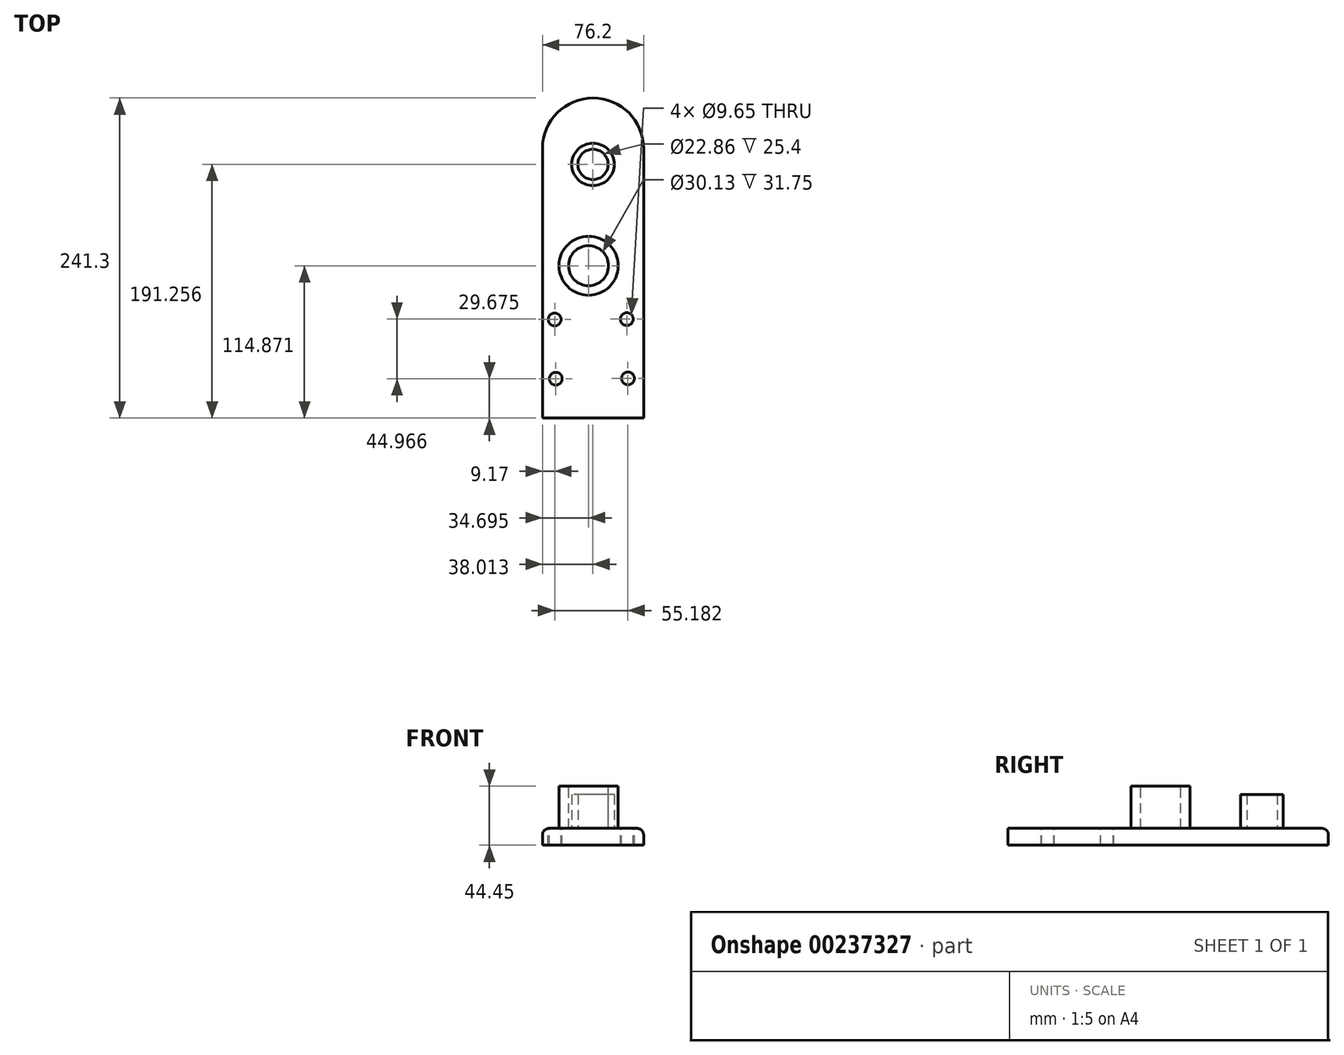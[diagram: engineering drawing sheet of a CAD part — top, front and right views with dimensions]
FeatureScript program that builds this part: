
annotation { "Feature Type Name" : "Feature", "Feature Type Description" : "" }
export const myFeature = defineFeature(function(context is Context, id is Id, definition is map)
    precondition{}
    {
        {
            var Q0;
            Q0=qCreatedBy(makeId("Top.planeOp"),FACE);
            var sketch = newSketch(context, id + "F0", { "sketchPlane" : qUnion([Q0])});
            skLineSegment(sketch, "E0", {"start": v(-28.8, -157.51) * mm, "end": v(47.4, -157.51) * mm});
            skLineSegment(sketch, "E1", {"start": v(47.4, -157.51) * mm, "end": v(47.4, 45.69) * mm});
            skLineSegment(sketch, "E2", {"start": v(-28.8, -157.51) * mm, "end": v(-28.8, 45.69) * mm});
            skArc(sketch, "E3", {"start": v(47.4, 45.69) * mm, "mid": v(9.3, 83.79) * mm, "end": v(-28.8, 45.69) * mm});
            skSolve(sketch);
        }
        {
            var Q0;
            Q0=makeQuery(id+"F0.imprint","IMPRINT",FACE,{"disambiguationData":[TD([[makeQuery(id+"F0.imprint","IMPRINT",EDGE,{"derivedFrom":sQuery(id+"F0.wireOp",EDGE,"E0")}),1.0]])]});
            extrude(context, id + "F1", {"entities" : qUnion([Q0]), "depth" : 12.7 * mm});
        }
        {
            var Q0;
            Q0=makeQuery(id+"F1.opExtrude","CAP_FACE",FACE,{"disambiguationData":[OSD([sQuery(id+"F0.wireOp",EDGE,"E0"),sQuery(id+"F0.wireOp",EDGE,"E1"),sQuery(id+"F0.wireOp",EDGE,"E2"),sQuery(id+"F0.wireOp",EDGE,"E3")])],"isStart":false});
            var sketch = newSketch(context, id + "F2", { "sketchPlane" : qUnion([Q0])});
            skCircle(sketch, "E4", {"center": v(-18.81, -127.83) * mm, "radius": 4.83 * mm});
            skCircle(sketch, "E5", {"center": v(35.54, -127.56) * mm, "radius": 4.83 * mm});
            skCircle(sketch, "E6", {"center": v(-19.64, -83.14) * mm, "radius": 4.83 * mm});
            skCircle(sketch, "E7", {"center": v(34.72, -82.87) * mm, "radius": 4.83 * mm});
            skSolve(sketch);
        }
        {
            var Q0;
            Q0 = qSketchRegion(id + "F2", true);
            extrude(context, id + "F3", {"entities" : qUnion([Q0]), "operationType" : NewBodyOperationType.REMOVE, "endBound" : BoundingType.THROUGH_ALL, "oppositeDirection" : true, "depth" : 25.4 * mm});
        }
        {
            var Q0;
            Q0=makeQuery(id+"F1.opExtrude","CAP_FACE",FACE,{"disambiguationData":[OSD([sQuery(id+"F0.wireOp",EDGE,"E0"),sQuery(id+"F0.wireOp",EDGE,"E1"),sQuery(id+"F0.wireOp",EDGE,"E2"),sQuery(id+"F0.wireOp",EDGE,"E3")])],"isStart":false});
            var sketch = newSketch(context, id + "F4", { "sketchPlane" : qUnion([Q0])});
            skCircle(sketch, "E8", {"center": v(5.88, -42.64) * mm, "radius": 22.23 * mm});
            skCircle(sketch, "E9", {"center": v(5.88, -42.64) * mm, "radius": 25.4 * mm});
            skSolve(sketch);
        }
        {
            var Q0;
            Q0=makeQuery(id+"F4.imprint","IMPRINT",FACE,{"disambiguationData":[TD([[makeQuery(id+"F4.imprint","IMPRINT",EDGE,{"derivedFrom":sQuery(id+"F4.wireOp",EDGE,"E8")}),1.0]])]});
            extrude(context, id + "F5", {"entities" : qUnion([Q0]), "operationType" : NewBodyOperationType.ADD, "depth" : 31.75 * mm});
        }
        {
            var Q0;
            {var subQ0=sQuery(id+"F0.wireOp",EDGE,"E3");var subQ1=sQuery(id+"F0.wireOp",EDGE,"E2");var subQ2=sQuery(id+"F0.wireOp",EDGE,"E1");var subQ3=sQuery(id+"F0.wireOp",EDGE,"E0");Q0=makeQuery(id+"F5.boolean.opBoolean","SPLIT",FACE,{"disambiguationData":[TD([makeQuery(id+"F1.opExtrude","SWEPT_FACE",FACE,{"disambiguationData":[OSD([subQ3])]})])],"derivedFrom":makeQuery(id+"F1.opExtrude","CAP_FACE",FACE,{"disambiguationData":[OSD([subQ3,subQ2,subQ1,subQ0])],"isStart":false})});}
            var sketch = newSketch(context, id + "F6", { "sketchPlane" : qUnion([Q0])});
            skCircle(sketch, "E10", {"center": v(9.2, 33.75) * mm, "radius": 16 * mm});
            skCircle(sketch, "E11", {"center": v(9.2, 33.75) * mm, "radius": 11.43 * mm});
            skSolve(sketch);
        }
        {
            var Q0;
            Q0 = qSketchRegion(id + "F6", true);
            extrude(context, id + "F7", {"entities" : qUnion([Q0]), "operationType" : NewBodyOperationType.ADD, "depth" : 25.4 * mm});
        }
        {
            var Q0;
            Q0=makeQuery(id+"F5.opExtrude","CAP_FACE",FACE,{"disambiguationData":[OSD([sQuery(id+"F4.wireOp",EDGE,"E8")])],"isStart":false});
            var sketch = newSketch(context, id + "F8", { "sketchPlane" : qUnion([Q0])});
            skCircle(sketch, "E12", {"center": v(5.88, -42.64) * mm, "radius": 15.07 * mm});
            skSolve(sketch);
        }
        {
            var Q0;
            Q0 = qSketchRegion(id + "F8", true);
            extrude(context, id + "F9", {"entities" : qUnion([Q0]), "operationType" : NewBodyOperationType.REMOVE, "oppositeDirection" : true, "depth" : 31.75 * mm});
        }
        {
            var Q0;
            Q0=makeQuery(id+"F1.opExtrude","CAP_EDGE",EDGE,{"disambiguationData":[OSD([sQuery(id+"F0.wireOp",EDGE,"E1")])],"isStart":false});
            fillet(context, id + "F10", {"entities" : qUnion([Q0]), "radius" : 5.08 * mm, "tangentPropagation" : true, "allowEdgeOverflow" : false});
        }
    });
